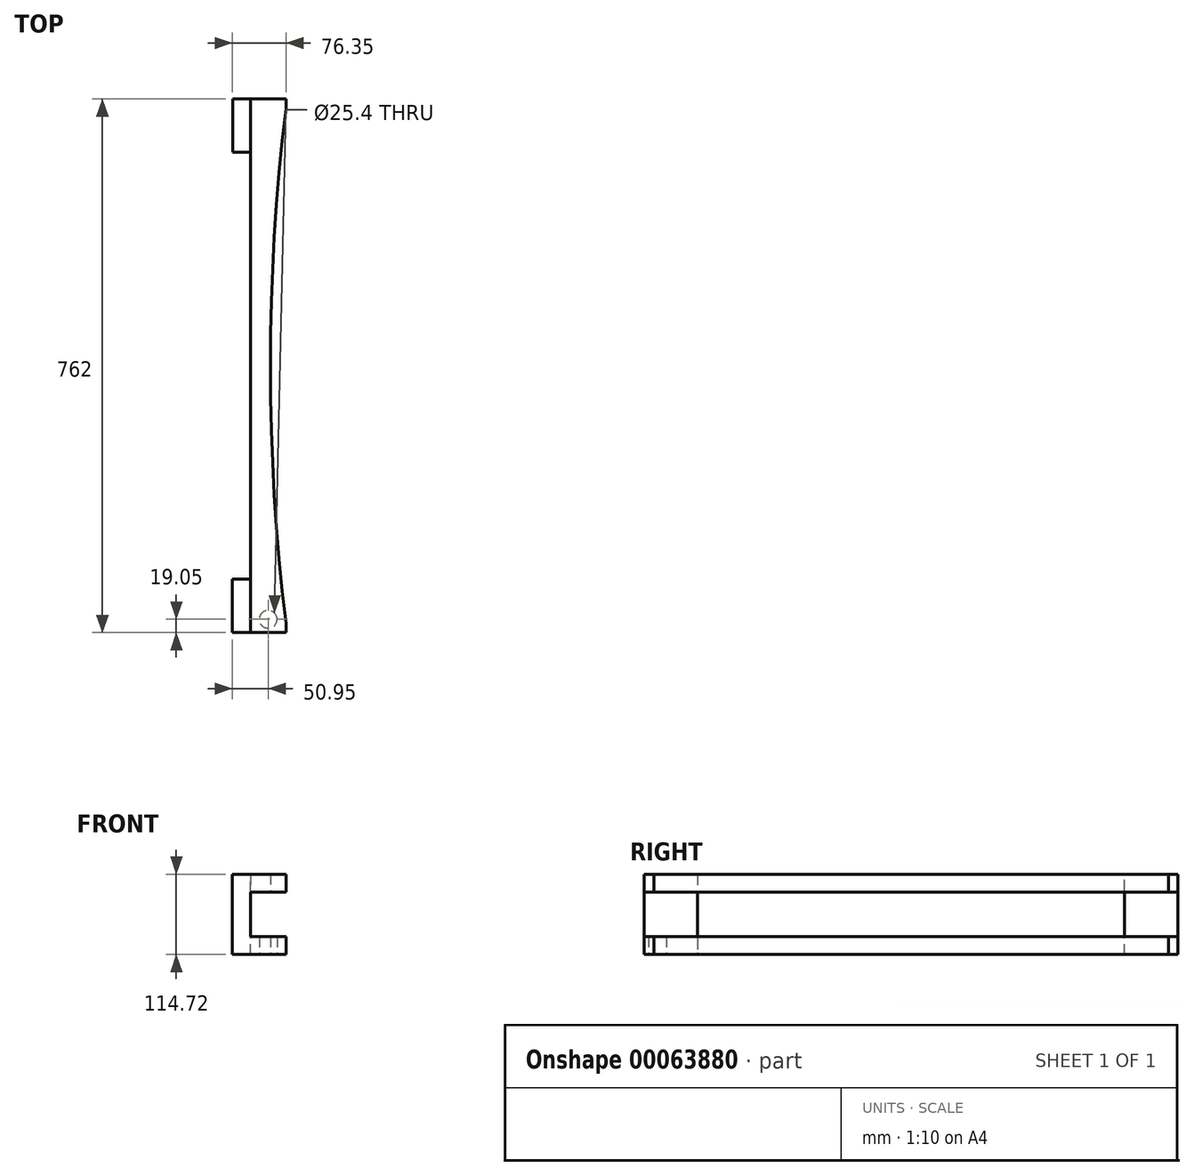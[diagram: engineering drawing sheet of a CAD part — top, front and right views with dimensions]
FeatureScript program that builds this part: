
annotation { "Feature Type Name" : "Feature", "Feature Type Description" : "" }
export const myFeature = defineFeature(function(context is Context, id is Id, definition is map)
    precondition{}
    {
        {
            var Q0;
            Q0=qCreatedBy(makeId("Front.planeOp"),FACE);
            var sketch = newSketch(context, id + "F0", { "sketchPlane" : qUnion([Q0])});
            skLineSegment(sketch, "E0.bottom", {"start": v(0, 0) * mm, "end": v(50.8, 0) * mm});
            skLineSegment(sketch, "E0.top", {"start": v(0, 25.4) * mm, "end": v(50.8, 25.4) * mm});
            skLineSegment(sketch, "E0.left", {"start": v(0, 0) * mm, "end": v(0, 25.4) * mm});
            skLineSegment(sketch, "E0.right", {"start": v(50.8, 0) * mm, "end": v(50.8, 25.4) * mm});
            skSolve(sketch);
        }
        {
            var Q0;
            Q0=makeQuery(id+"F0.imprint","IMPRINT",FACE,{"disambiguationData":[TD([[makeQuery(id+"F0.imprint","IMPRINT",EDGE,{"derivedFrom":sQuery(id+"F0.wireOp",EDGE,"E0.bottom")}),1.0]])]});
            extrude(context, id + "F1", {"entities" : qUnion([Q0]), "oppositeDirection" : true, "depth" : 762 * mm});
        }
        {
            var Q0;
            Q0=qCreatedBy(makeId("Front.planeOp"),FACE);
            var sketch = newSketch(context, id + "F2", { "sketchPlane" : qUnion([Q0])});
            skLineSegment(sketch, "E1.bottom", {"start": v(0, 25.03) * mm, "end": v(-25.55, 25.03) * mm});
            skLineSegment(sketch, "E1.top", {"start": v(0, -89.17) * mm, "end": v(-25.55, -89.17) * mm});
            skLineSegment(sketch, "E1.left", {"start": v(0, 25.03) * mm, "end": v(0, -89.17) * mm});
            skLineSegment(sketch, "E1.right", {"start": v(-25.55, 25.03) * mm, "end": v(-25.55, -89.17) * mm});
            skSolve(sketch);
        }
        {
            var Q0;
            Q0 = qSketchRegion(id + "F2", true);
            extrude(context, id + "F3", {"entities" : qUnion([Q0]), "operationType" : NewBodyOperationType.ADD, "oppositeDirection" : true, "depth" : 76.2 * mm});
        }
        {
            var Q0;
            Q0=qCreatedBy(makeId("Front.planeOp"),FACE);
            var sketch = newSketch(context, id + "F4", { "sketchPlane" : qUnion([Q0])});
            skPoint(sketch, "E2.0", {"position": v(-25.55, -89.17) * mm});
            skLineSegment(sketch, "E3.bottom", {"start": v(0, -89.32) * mm, "end": v(50.8, -89.32) * mm});
            skLineSegment(sketch, "E3.top", {"start": v(0, -63.85) * mm, "end": v(50.8, -63.85) * mm});
            skLineSegment(sketch, "E3.left", {"start": v(0, -89.32) * mm, "end": v(0, -63.85) * mm});
            skLineSegment(sketch, "E3.right", {"start": v(50.8, -89.32) * mm, "end": v(50.8, -63.85) * mm});
            skSolve(sketch);
        }
        {
            var Q0;
            Q0 = qSketchRegion(id + "F4", true);
            extrude(context, id + "F5", {"entities" : qUnion([Q0]), "operationType" : NewBodyOperationType.ADD, "oppositeDirection" : true, "depth" : 762 * mm});
        }
        {
            var Q0;
            Q0=makeQuery(id+"F5.opExtrude","CAP_FACE",FACE,{"disambiguationData":[OSD([sQuery(id+"F4.wireOp",EDGE,"E3.bottom"),sQuery(id+"F4.wireOp",EDGE,"E3.top"),sQuery(id+"F4.wireOp",EDGE,"E3.left"),sQuery(id+"F4.wireOp",EDGE,"E3.right")])],"isStart":false});
            var sketch = newSketch(context, id + "F6", { "sketchPlane" : qUnion([Q0])});
            skLineSegment(sketch, "E4.bottom", {"start": v(0, -89.32) * mm, "end": v(25.4, -89.32) * mm});
            skLineSegment(sketch, "E4.top", {"start": v(0, 24.98) * mm, "end": v(25.4, 24.98) * mm});
            skLineSegment(sketch, "E4.left", {"start": v(0, -89.32) * mm, "end": v(0, 25.35) * mm});
            skLineSegment(sketch, "E4.right", {"start": v(25.4, -89.32) * mm, "end": v(25.4, 24.98) * mm});
            skSolve(sketch);
        }
        {
            var Q0;
            {var subQ1=sQuery(id+"F6.wireOp",EDGE,"E4.bottom");Q0=makeQuery(id+"F6.imprint","IMPRINT",FACE,{"disambiguationData":[TD([[makeQuery(id+"F6.imprint","IMPRINT",EDGE,{"derivedFrom":subQ1}),1.0]])]});}
            extrude(context, id + "F7", {"entities" : qUnion([Q0]), "operationType" : NewBodyOperationType.ADD, "oppositeDirection" : true, "depth" : 76.2 * mm});
        }
        {
            var Q0;
            Q0=makeQuery(id+"F7.boolean.opBoolean","MERGE",FACE,{"derivedFrom":[makeQuery(id+"F5.opExtrude","SWEPT_FACE",FACE,{"disambiguationData":[OSD([sQuery(id+"F4.wireOp",EDGE,"E3.bottom")])]}),makeQuery(id+"F7.opExtrude","SWEPT_FACE",FACE,{"disambiguationData":[OSD([sQuery(id+"F6.wireOp",EDGE,"E4.bottom")])]})]});
            var sketch = newSketch(context, id + "F8", { "sketchPlane" : qUnion([Q0])});
            skCircle(sketch, "E5", {"center": v(3076.58, -381) * mm, "radius": 3048 * mm});
            skPoint(sketch, "E5.centerSnap0", {"position": v(50.8, -381) * mm});
            skSolve(sketch);
        }
        {
            var Q0;
            {var subQ0=sQuery(id+"F8.wireOp",EDGE,"E5");var subQ1=makeQuery(id+"F5.opExtrude","SWEPT_EDGE",EDGE,{"disambiguationData":[OSD([sQuery(id+"F4.wireOp",EDGE,"E3.bottom"),sQuery(id+"F4.wireOp",EDGE,"E3.right")])]});var subQ2=makeQuery(id+"F8.imprint","INTERSECT",VERTEX,{"disambiguationData":[OD(0.0)],"derivedFrom":[subQ1,subQ0]});Q0=makeQuery(id+"F8.imprint","IMPRINT",FACE,{"disambiguationData":[TD([[makeQuery(id+"F8.imprint","IMPRINT",EDGE,{"disambiguationData":[TD([[subQ2,1.0]])],"derivedFrom":subQ0}),1.0]])]});}
            var Q1;
            {var subQ0=sQuery(id+"F8.wireOp",EDGE,"E5");var subQ1=makeQuery(id+"F5.opExtrude","SWEPT_EDGE",EDGE,{"disambiguationData":[OSD([sQuery(id+"F4.wireOp",EDGE,"E3.bottom"),sQuery(id+"F4.wireOp",EDGE,"E3.right")])]});var subQ2=makeQuery(id+"F8.imprint","INTERSECT",VERTEX,{"disambiguationData":[OD(0.0)],"derivedFrom":[subQ1,subQ0]});Q1=makeQuery(id+"F8.imprint","IMPRINT",FACE,{"disambiguationData":[TD([[makeQuery(id+"F8.imprint","IMPRINT",EDGE,{"disambiguationData":[TD([[subQ2,-1.0]])],"derivedFrom":subQ0}),1.0]])]});}
            extrude(context, id + "F9", {"entities" : qUnion([Q0, Q1]), "operationType" : NewBodyOperationType.REMOVE, "endBound" : BoundingType.THROUGH_ALL, "oppositeDirection" : true, "depth" : 25.4 * mm});
        }
        {
            var Q0;
            Q0=makeQuery(id+"F7.boolean.opBoolean","MERGE",FACE,{"derivedFrom":[makeQuery(id+"F5.opExtrude","SWEPT_FACE",FACE,{"disambiguationData":[OSD([sQuery(id+"F4.wireOp",EDGE,"E3.bottom")])]}),makeQuery(id+"F7.opExtrude","SWEPT_FACE",FACE,{"disambiguationData":[OSD([sQuery(id+"F6.wireOp",EDGE,"E4.bottom")])]})]});
            var sketch = newSketch(context, id + "F10", { "sketchPlane" : qUnion([Q0])});
            skCircle(sketch, "E6", {"center": v(25.4, -19.05) * mm, "radius": 12.7 * mm});
            skSolve(sketch);
        }
        {
            var Q0;
            Q0=makeQuery(id+"F10.imprint","IMPRINT",FACE,{"disambiguationData":[TD([[makeQuery(id+"F10.imprint","IMPRINT",EDGE,{"derivedFrom":sQuery(id+"F10.wireOp",EDGE,"E6")}),1.0]])]});
            extrude(context, id + "F11", {"entities" : qUnion([Q0]), "operationType" : NewBodyOperationType.REMOVE, "endBound" : BoundingType.UP_TO_NEXT, "oppositeDirection" : true, "depth" : 25.4 * mm});
        }
    });
